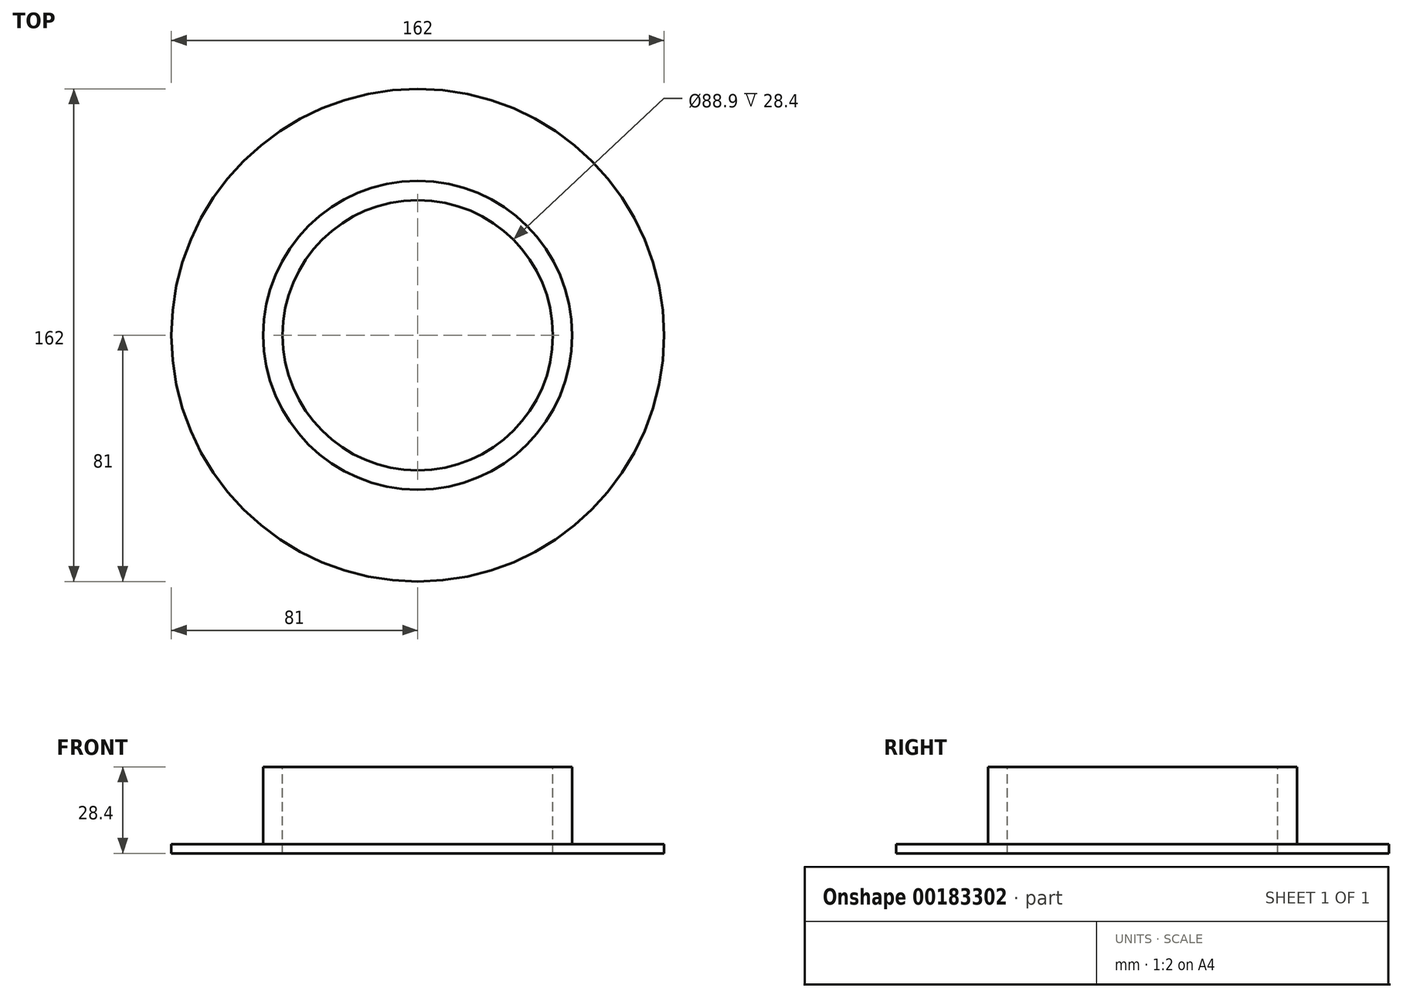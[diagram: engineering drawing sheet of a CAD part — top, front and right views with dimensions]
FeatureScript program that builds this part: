
annotation { "Feature Type Name" : "Feature", "Feature Type Description" : "" }
export const myFeature = defineFeature(function(context is Context, id is Id, definition is map)
    precondition{}
    {
        {
            var Q0;
            Q0=qCreatedBy(makeId("Top.planeOp"),FACE);
            var sketch = newSketch(context, id + "F0", { "sketchPlane" : qUnion([Q0])});
            skCircle(sketch, "E0", {"center": v(0, 0) * mm, "radius": 81 * mm});
            skSolve(sketch);
        }
        {
            var Q0;
            Q0=makeQuery(id+"F0.imprint","IMPRINT",FACE,{"disambiguationData":[TD([[makeQuery(id+"F0.imprint","IMPRINT",EDGE,{"derivedFrom":sQuery(id+"F0.wireOp",EDGE,"E0")}),1.0]])]});
            extrude(context, id + "F1", {"entities" : qUnion([Q0]), "depth" : 3 * mm});
        }
        {
            var Q0;
            Q0=makeQuery(id+"F1.opExtrude","CAP_FACE",FACE,{"disambiguationData":[OSD([sQuery(id+"F0.wireOp",EDGE,"E0")])],"isStart":false});
            var sketch = newSketch(context, id + "F2", { "sketchPlane" : qUnion([Q0])});
            skCircle(sketch, "E1", {"center": v(0, 0) * mm, "radius": 50.8 * mm});
            skSolve(sketch);
        }
        {
            var Q0;
            Q0=makeQuery(id+"F2.imprint","IMPRINT",FACE,{"disambiguationData":[TD([[makeQuery(id+"F2.imprint","IMPRINT",EDGE,{"derivedFrom":sQuery(id+"F2.wireOp",EDGE,"E1")}),1.0]])]});
            extrude(context, id + "F3", {"entities" : qUnion([Q0]), "operationType" : NewBodyOperationType.ADD, "depth" : 25.4 * mm});
        }
        {
            var Q0;
            Q0=makeQuery(id+"F3.opExtrude","CAP_FACE",FACE,{"disambiguationData":[OSD([sQuery(id+"F2.wireOp",EDGE,"E1")])],"isStart":false});
            var sketch = newSketch(context, id + "F4", { "sketchPlane" : qUnion([Q0])});
            skCircle(sketch, "E2", {"center": v(0, 0) * mm, "radius": 44.45 * mm});
            skSolve(sketch);
        }
        {
            var Q0;
            Q0=makeQuery(id+"F4.imprint","IMPRINT",FACE,{"disambiguationData":[TD([[makeQuery(id+"F4.imprint","IMPRINT",EDGE,{"derivedFrom":sQuery(id+"F4.wireOp",EDGE,"E2")}),1.0]])]});
            extrude(context, id + "F5", {"entities" : qUnion([Q0]), "operationType" : NewBodyOperationType.REMOVE, "endBound" : BoundingType.THROUGH_ALL, "oppositeDirection" : true, "depth" : 25.4 * mm});
        }
    });
